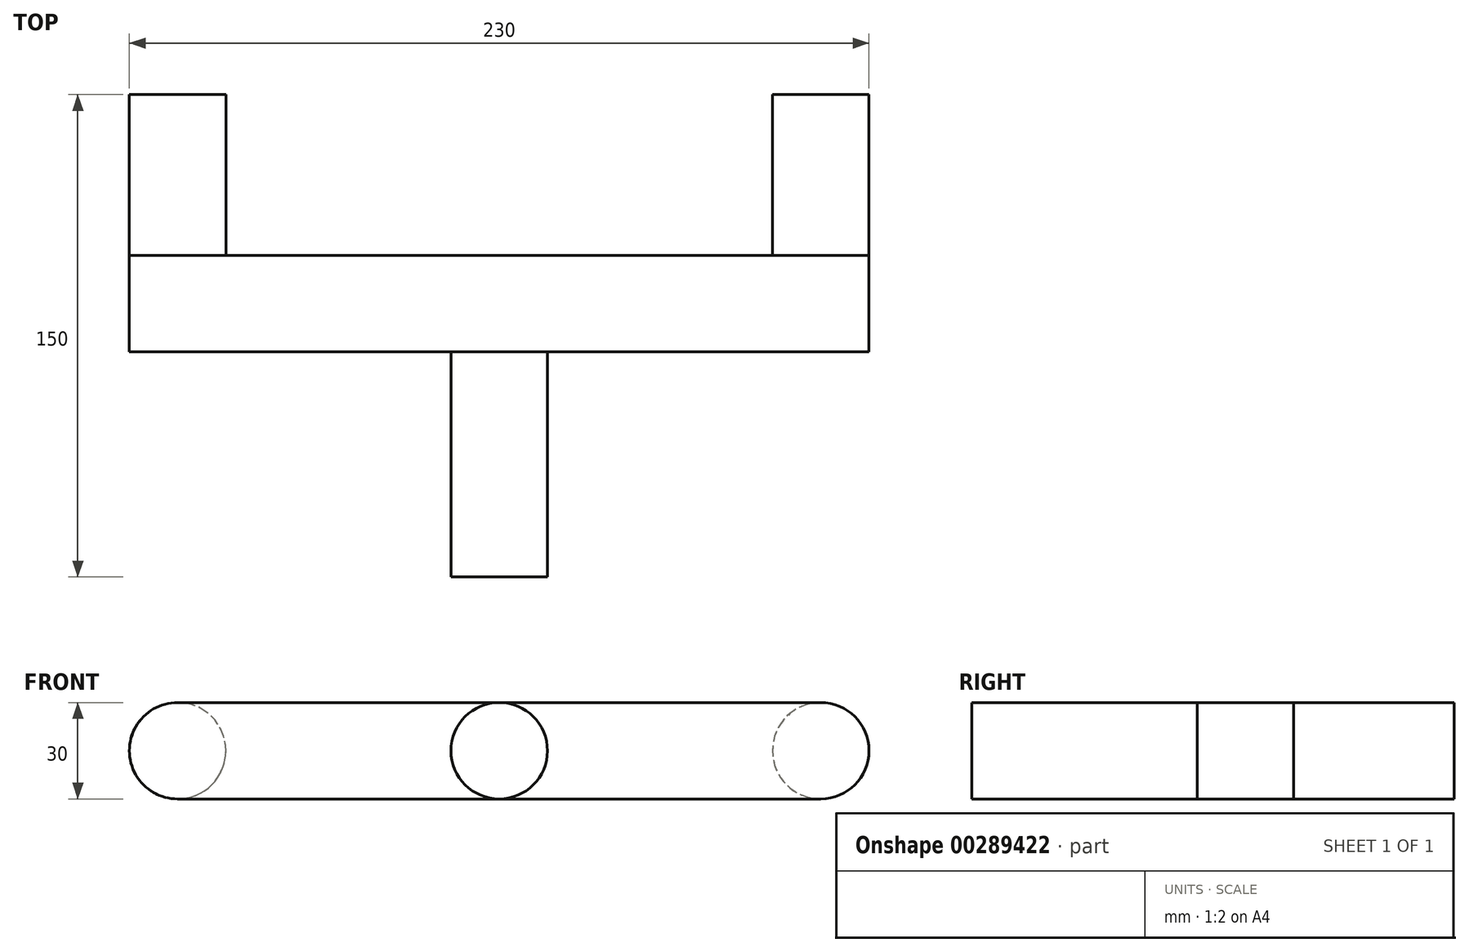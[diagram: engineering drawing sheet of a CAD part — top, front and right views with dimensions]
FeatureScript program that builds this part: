
annotation { "Feature Type Name" : "Feature", "Feature Type Description" : "" }
export const myFeature = defineFeature(function(context is Context, id is Id, definition is map)
    precondition{}
    {
        {
            var Q0;
            Q0=qCreatedBy(makeId("Front.planeOp"),FACE);
            var sketch = newSketch(context, id + "F0", { "sketchPlane" : qUnion([Q0])});
            skCircle(sketch, "E0", {"center": v(-100, 0) * mm, "radius": 15 * mm});
            skCircle(sketch, "E1", {"center": v(100, 0) * mm, "radius": 15 * mm});
            skLineSegment(sketch, "E2", {"start": v(0, 0) * mm, "end": v(-100, 0) * mm});
            skLineSegment(sketch, "E3", {"start": v(0, 0) * mm, "end": v(100, 0) * mm});
            skSolve(sketch);
        }
        {
            var Q0;
            Q0=makeQuery(id+"F0.imprint","IMPRINT",FACE,{"disambiguationData":[TD([[makeQuery(id+"F0.imprint","IMPRINT",EDGE,{"derivedFrom":sQuery(id+"F0.wireOp",EDGE,"E0")}),1.0]])]});
            var Q1;
            Q1=makeQuery(id+"F0.imprint","IMPRINT",FACE,{"disambiguationData":[TD([[makeQuery(id+"F0.imprint","IMPRINT",EDGE,{"derivedFrom":sQuery(id+"F0.wireOp",EDGE,"E1")}),1.0]])]});
            extrude(context, id + "F1", {"entities" : qUnion([Q0, Q1]), "depth" : 50 * mm});
        }
        {
            var Q0;
            Q0=qCreatedBy(makeId("Front.planeOp"),FACE);
            cPlane(context, id + "F2", {"entities" : qUnion([Q0]), "cplaneType" : CPlaneType.OFFSET, "offset" : 50 * mm, "width" : 150 * mm, "height" : 150 * mm});
        }
        {
            var Q0;
            Q0=qCreatedBy(id+"F2.planeOp",FACE);
            var sketch = newSketch(context, id + "F3", { "sketchPlane" : qUnion([Q0])});
            skCircle(sketch, "E4", {"center": v(-100, 0) * mm, "radius": 15 * mm});
            skCircle(sketch, "E5", {"center": v(100, 0) * mm, "radius": 15 * mm});
            skLineSegment(sketch, "E6.bottom", {"start": v(-100, 15) * mm, "end": v(100.02, 15) * mm});
            skLineSegment(sketch, "E6.top", {"start": v(-100, -15) * mm, "end": v(100.02, -15) * mm});
            skSolve(sketch);
        }
        {
            var Q0;
            {var subQ0=sQuery(id+"F3.wireOp",EDGE,"E4");var subQ1=makeQuery(id+"F3.imprint","INTERSECT",VERTEX,{"derivedFrom":[subQ0,sQuery(id+"F3.wireOp",EDGE,"E6.bottom")]});Q0=makeQuery(id+"F3.imprint","IMPRINT",FACE,{"disambiguationData":[TD([[makeQuery(id+"F3.imprint","IMPRINT",EDGE,{"disambiguationData":[TD([[subQ1,-1.0]])],"derivedFrom":subQ0}),1.0]])]});}
            var Q1;
            {var subQ0=sQuery(id+"F3.wireOp",EDGE,"E5");var subQ1=makeQuery(id+"F3.imprint","INTERSECT",VERTEX,{"derivedFrom":[subQ0,sQuery(id+"F3.wireOp",EDGE,"E6.bottom")]});Q1=makeQuery(id+"F3.imprint","IMPRINT",FACE,{"disambiguationData":[TD([[makeQuery(id+"F3.imprint","IMPRINT",EDGE,{"disambiguationData":[TD([[subQ1,-1.0]])],"derivedFrom":subQ0}),1.0]])]});}
            var Q2;
            {var subQ0=sQuery(id+"F3.wireOp",EDGE,"E6.bottom");Q2=makeQuery(id+"F3.imprint","IMPRINT",FACE,{"disambiguationData":[TD([[makeQuery(id+"F3.imprint","IMPRINT",EDGE,{"derivedFrom":subQ0}),-1.0]])]});}
            extrude(context, id + "F4", {"entities" : qUnion([Q0, Q1, Q2]), "depth" : 30 * mm});
        }
        {
            var Q0;
            Q0=qCreatedBy(id+"F2.planeOp",FACE);
            var sketch = newSketch(context, id + "F5", { "sketchPlane" : qUnion([Q0])});
            skCircle(sketch, "E7", {"center": v(0, 0) * mm, "radius": 15 * mm});
            skSolve(sketch);
        }
        {
            var Q0;
            Q0 = qSketchRegion(id + "F5", true);
            extrude(context, id + "F6", {"entities" : qUnion([Q0]), "operationType" : NewBodyOperationType.ADD, "depth" : 100 * mm});
        }
    });
